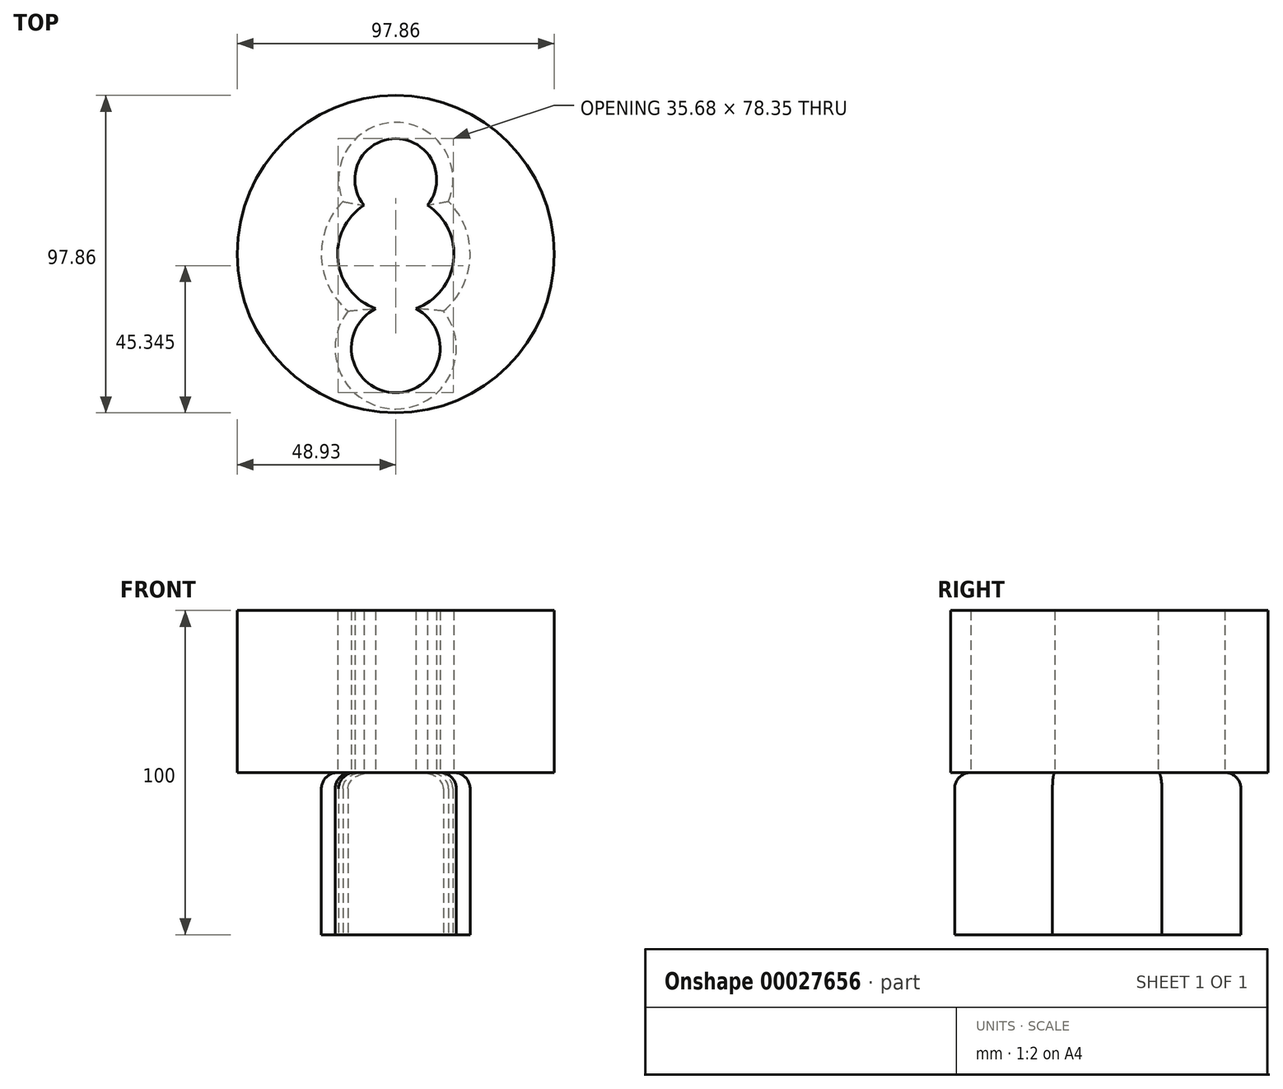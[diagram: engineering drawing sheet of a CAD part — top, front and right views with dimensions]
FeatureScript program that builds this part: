
annotation { "Feature Type Name" : "Feature", "Feature Type Description" : "" }
export const myFeature = defineFeature(function(context is Context, id is Id, definition is map)
    precondition{}
    {
        {
            var Q0;
            Q0=qCreatedBy(makeId("Top.planeOp"),FACE);
            var sketch = newSketch(context, id + "F0", { "sketchPlane" : qUnion([Q0])});
            skCircle(sketch, "E0", {"center": v(0, 0) * mm, "radius": 22.95 * mm});
            skCircle(sketch, "E1", {"center": v(0, -29.06) * mm, "radius": 18.7 * mm});
            skCircle(sketch, "E2", {"center": v(0, 22.95) * mm, "radius": 17.63 * mm});
            skSolve(sketch);
        }
        {
            var Q0;
            Q0 = qSketchRegion(id + "F0", true);
            extrude(context, id + "F1", {"entities" : qUnion([Q0]), "depth" : 50 * mm});
        }
        {
            var Q0;
            Q0=makeQuery(id+"F1.opExtrude","CAP_EDGE",EDGE,{"disambiguationData":[OSD([sQuery(id+"F0.wireOp",EDGE,"E1")])],"isStart":false});
            fillet(context, id + "F2", {"entities" : qUnion([Q0]), "radius" : 5 * mm, "tangentPropagation" : true, "allowEdgeOverflow" : false});
        }
        {
            var Q0;
            {var subQ0=sQuery(id+"F0.wireOp",EDGE,"E0");Q0=makeQuery(id+"F1.opExtrude","CAP_EDGE",EDGE,{"disambiguationData":[OSD([subQ0]),TDD([makeQuery(id+"F0.imprint","IMPRINT",EDGE,{"disambiguationData":[TD([[makeQuery(id+"F0.imprint","INTERSECT",VERTEX,{"disambiguationData":[OD(1.0)],"derivedFrom":[subQ0,sQuery(id+"F0.wireOp",EDGE,"E2")]}),1.0]])],"derivedFrom":subQ0})])],"isStart":false});}
            var Q1;
            Q1=makeQuery(id+"F1.opExtrude","CAP_EDGE",EDGE,{"disambiguationData":[OSD([sQuery(id+"F0.wireOp",EDGE,"E2")])],"isStart":false});
            var Q2;
            {var subQ0=sQuery(id+"F0.wireOp",EDGE,"E0");Q2=makeQuery(id+"F1.opExtrude","CAP_EDGE",EDGE,{"disambiguationData":[OSD([subQ0]),TDD([makeQuery(id+"F0.imprint","IMPRINT",EDGE,{"disambiguationData":[TD([[makeQuery(id+"F0.imprint","INTERSECT",VERTEX,{"disambiguationData":[OD(0.0)],"derivedFrom":[subQ0,sQuery(id+"F0.wireOp",EDGE,"E2")]}),-1.0]])],"derivedFrom":subQ0})])],"isStart":false});}
            fillet(context, id + "F3", {"entities" : qUnion([Q0, Q1, Q2]), "radius" : 5 * mm, "tangentPropagation" : true, "allowEdgeOverflow" : false});
        }
        {
            var Q0;
            Q0=makeQuery(id+"F1.opExtrude","CAP_FACE",FACE,{"disambiguationData":[OSD([sQuery(id+"F0.wireOp",EDGE,"E0"),sQuery(id+"F0.wireOp",EDGE,"E1"),sQuery(id+"F0.wireOp",EDGE,"E2")])],"isStart":false});
            var sketch = newSketch(context, id + "F4", { "sketchPlane" : qUnion([Q0])});
            skCircle(sketch, "E3", {"center": v(0, 0) * mm, "radius": 48.93 * mm});
            skSolve(sketch);
        }
        {
            var Q0;
            Q0=makeQuery(id+"F4.imprint","IMPRINT",FACE,{"disambiguationData":[TD([[makeQuery(id+"F4.imprint","IMPRINT",EDGE,{"derivedFrom":sQuery(id+"F4.wireOp",EDGE,"E3")}),1.0]])]});
            extrude(context, id + "F5", {"entities" : qUnion([Q0]), "depth" : 50 * mm});
        }
    });
